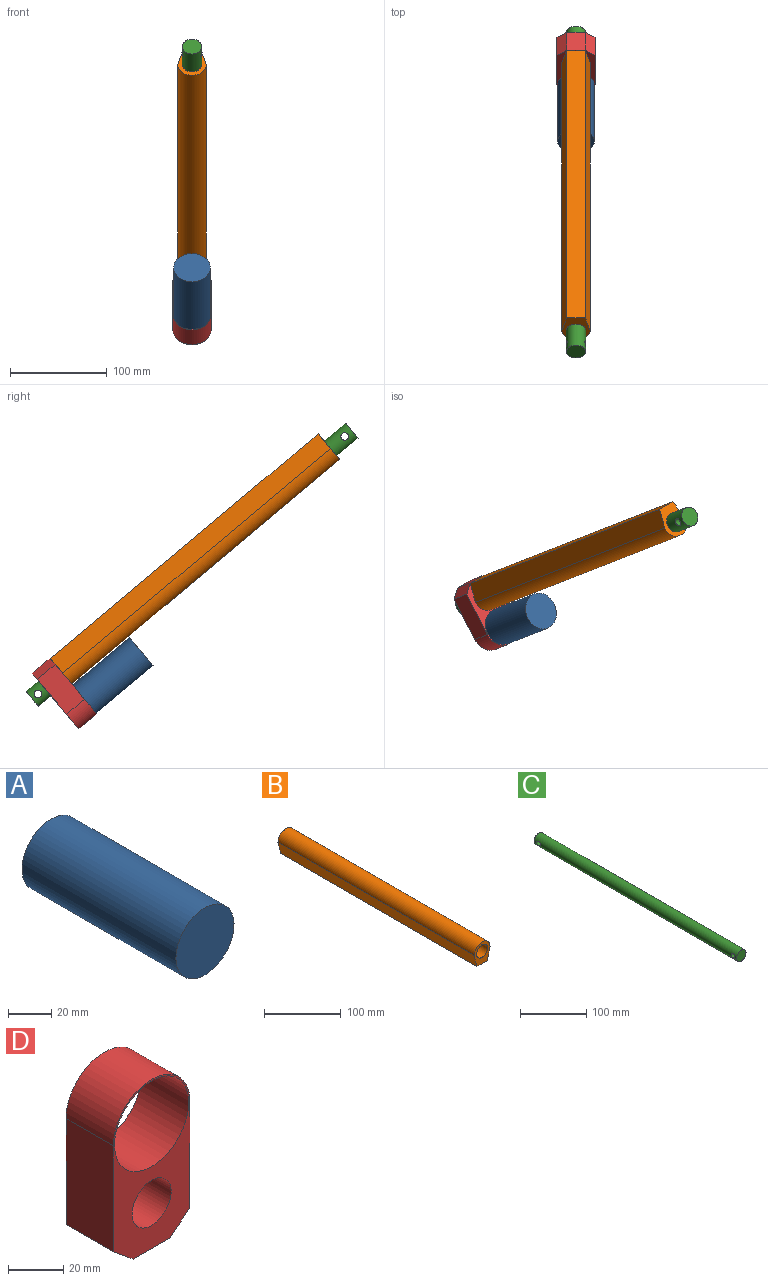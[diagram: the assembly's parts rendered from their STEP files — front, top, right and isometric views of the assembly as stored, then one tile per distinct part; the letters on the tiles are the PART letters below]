
ASSEMBLY  parts=4 mates=3
PART A: 3 faces, bbox 38.1x101x38.1 mm
  f0: cylinder r=19.05mm len=100.97mm, axis (0,1,0), area 12085mm2, adj f1,f2
  f1: plane 38.1x38.1mm, normal (0,-1,0), area 1140.1mm2, adj f0
  f2: plane 38.1x38.1mm, normal (0,1,0), area 1140.1mm2, adj f0
PART B: 7 faces, bbox 29.2x362x34.4 mm
  f0: cylinder r=14.61mm len=361.95mm, axis (0,-1,0), area 16607.3mm2, adj f1,f4,f5,f6
  f1: plane 361.95x19.81mm, normal (-0.97,0,-0.25), area 7402.9mm2, adj f0,f2,f5,f6
  f2: plane 361.95x19.05mm, normal (0,0,-1), area 6895.1mm2, adj f1,f4,f5,f6
  f3: cylinder r=10.03mm len=361.95mm, axis (0,-1,0), area 22817mm2, adj f5,f6
  f4: plane 361.95x19.81mm, normal (0.97,0,-0.25), area 7402.9mm2, adj f0,f2,f5,f6
  f5: plane 34.42x29.21mm, normal (0,1,0), area 496.9mm2, adj f0,f1,f2,f3,f4
  f6: plane 34.42x29.21mm, normal (0,-1,0), area 496.9mm2, adj f0,f1,f2,f3,f4
PART C: 5 faces, bbox 20.1x431.9x20.1 mm
  f0: cylinder r=10.03mm len=431.93mm, axis (0,1,0), area 27026.1mm2, adj f1,f2,f3,f4
  f1: plane 20.07x20.07mm, normal (0,1,0), area 316.2mm2, adj f0
  f2: plane 20.07x20.07mm, normal (0,-1,0), area 316.2mm2, adj f0
  f3: cylinder r=3.97mm len=20.07mm, axis (-1,0,0), area 480.2mm2, adj f0
  f4: cylinder r=3.97mm len=20.07mm, axis (1,0,0), area 480.2mm2, adj f0
PART D: 10 faces, bbox 39.4x24.3x75.1 mm
  f0: plane 47.12x24.26mm, normal (1,0,0), area 1142.9mm2, adj f1,f6,f8,f9
  f1: cylinder r=19.69mm len=39.37mm, axis (0,1,0), area 1500.1mm2, adj f0,f2,f8,f9
  f2: plane 47.12x24.26mm, normal (-1,0,0), area 1142.9mm2, adj f1,f3,f8,f9
  f3: plane 24.26x10.16mm, normal (-0.63,0,-0.78), area 317.5mm2, adj f2,f4,f8,f9
  f4: plane 24.26x19.05mm, normal (0,0,-1), area 462.1mm2, adj f3,f6,f8,f9
  f5: cylinder r=19.05mm len=38.1mm, axis (0,1,0), area 2903.4mm2, adj f8,f9
  f6: plane 24.26x10.16mm, normal (0.63,0,-0.78), area 317.5mm2, adj f0,f4,f8,f9
  f7: cylinder r=10.03mm len=24.26mm, axis (0,1,0), area 1529.1mm2, adj f8,f9
  f8: plane 75.06x39.37mm, normal (0,-1,0), area 1248.5mm2, adj f0,f1,f2,f3,f4,f5,f6,f7
  f9: plane 75.06x39.37mm, normal (0,1,0), area 1248.5mm2, adj f0,f1,f2,f3,f4,f5,f6,f7
PLACE A rot(axis=(1,0,0),140deg) t=(236.45,842.3,-234.89)mm
PLACE B rot(axis=(1,0,0),140deg) t=(236.45,912.59,-270.46)mm
PLACE C rot(axis=(1,0,0),140deg) t=(236.45,727.84,-128.54)mm
PLACE D rot(axis=(1,0,0),140deg) t=(236.45,901.44,-283.74)mm
MATE fastened D.f7 <-> B.f3  axis (0,-0.77,0.64) through (236.45,912.59,-270.46)mm
MATE fastened A.f0 <-> D.f1  axis (0,0.77,-0.64) through (236.45,908.56,-313)mm
MATE slider C.f0 <-> B.f0  axis (0,-0.77,0.64) through (236.45,778.67,-158.1)mm
